# Revit family: BSK_ZEPHYR_WALL MOUNTED_LOD400
name_source: partatom
category: Mechanical Equipment
units: mm (PartAtom-declared; Revit-internal decimal feet)

## family parameters
Always vertical = Yes
Cut with Voids When Loaded = No
Host = Wall
Maintain Annotation Orientation = No
OmniClass Number = 23.75.00.00
OmniClass Title = Climate Control (HVAC)
Part Type = Normal
Room Calculation Point = No
Round Connector Dimension = Use Diameter
Shared = No

## types (1)
- TYPE 1
    Air Flow Direction = Bottom
    Cap Height = 220 mm  [stored 0.721785 ft]
    Cap Material Exterior = Aluminum
    Cap Material Interior = Aluminum
    Cap Width = 220 mm  [stored 0.721785 ft]
    Clearence Bottom = 200 mm  [stored 0.656168 ft]
    Clearence Face = 300 mm
    Clearence Side = 100 mm  [stored 0.328084 ft]
    Clearence Top = 50 mm  [stored 0.164042 ft]
    Default Elevation = 0 mm  [stored 0 ft]
    Frequency = 50/60Hz
    IPX4 = A+
    Manufacturer = BSK Havalandırma Ekipmanları AŞ
    Max Electrical Power = 3 W
    Max Thermal Efficiency = 90%
    Model = Zephyr
    Night Mode Air Flow = 15.0 CMH
    Night Mode Sound Power = 22 dB
    Operating Temperature = -25 / +50 C
    Reservation Size (Diameter) = 170 mm
    SEC Class = A+
    Speed 1 Air Flow = 30.0 CMH
    Speed 1 Sound Power = 26 dB
    Speed 2 Air Flow = 45.0 CMH
    Speed 2 Sound Power = 40 dB
    Speed 3 Air Flow = 60.0 CMH
    Speed 3 Sound Power = 48 dB
    Supply Voltage = 110/230V
    Website = www.bskhvac.com.tr

note: [stored X ft] marks values corroborated as IEEE doubles in the binary element streams (Revit-internal decimal feet)

## geometry (parser evidence)
native form markers: Sweep x4
no freeform markers — native parametric forms only
